# Revit family: Trägerklammer F3-M 8, zweiteilig
name_source: partatom
category: HLS-Bauteile
units: mm (PartAtom-declared; Revit-internal decimal feet)

## family parameters
Basisbauteil = Fläche
Beim Laden mit Abzugskörper schneiden = Nein
Bemaßung runder Anschluss = Durchmesser verwenden
Beschriftungsausrichtung beibehalten = Nein
Gemeinsam genutzt = Ja
Raumberechnungspunkt = Nein
Teiletyp = Normal

## types (1)
- Trägerklammer F3/M8
    Artikelnummer = 0579613
    Befestigung = mit Durchgangsloch
    DF1 = 10 mm  [stored 0.0328084 ft]
    EAN = 4250928414748
    Fabrikat = Lindapter
    Firma = MEFA Befestigungs- und Montagesysteme GmbH
    Gewicht = 0.10 kg
    Gewicht pro Bauteil = 0.10 kg
    Gewinde = für M8
    Kurztext1 = Trägerklammer Guss F3
    Kurztext2 = Klemmbereich 1 - 25 mm Loch für M8
    Material = Temperguss
    Mengeneinheit = St
    Oberflaeche = feuerstückverzinkt
    Sicherheitsfaktor = 4
    Stärke = 8 mm  [stored 0.0262467 ft]
    Vorgabe-Ansicht = 1219 mm
    max Klemmdicke = 25 mm  [stored 0.082021 ft]
    max. zul. Last = 0.20 kip
    min. Klemmdicke = 1 mm
    vpe = 1

note: [stored X ft] marks values corroborated as IEEE doubles in the binary element streams (Revit-internal decimal feet)
